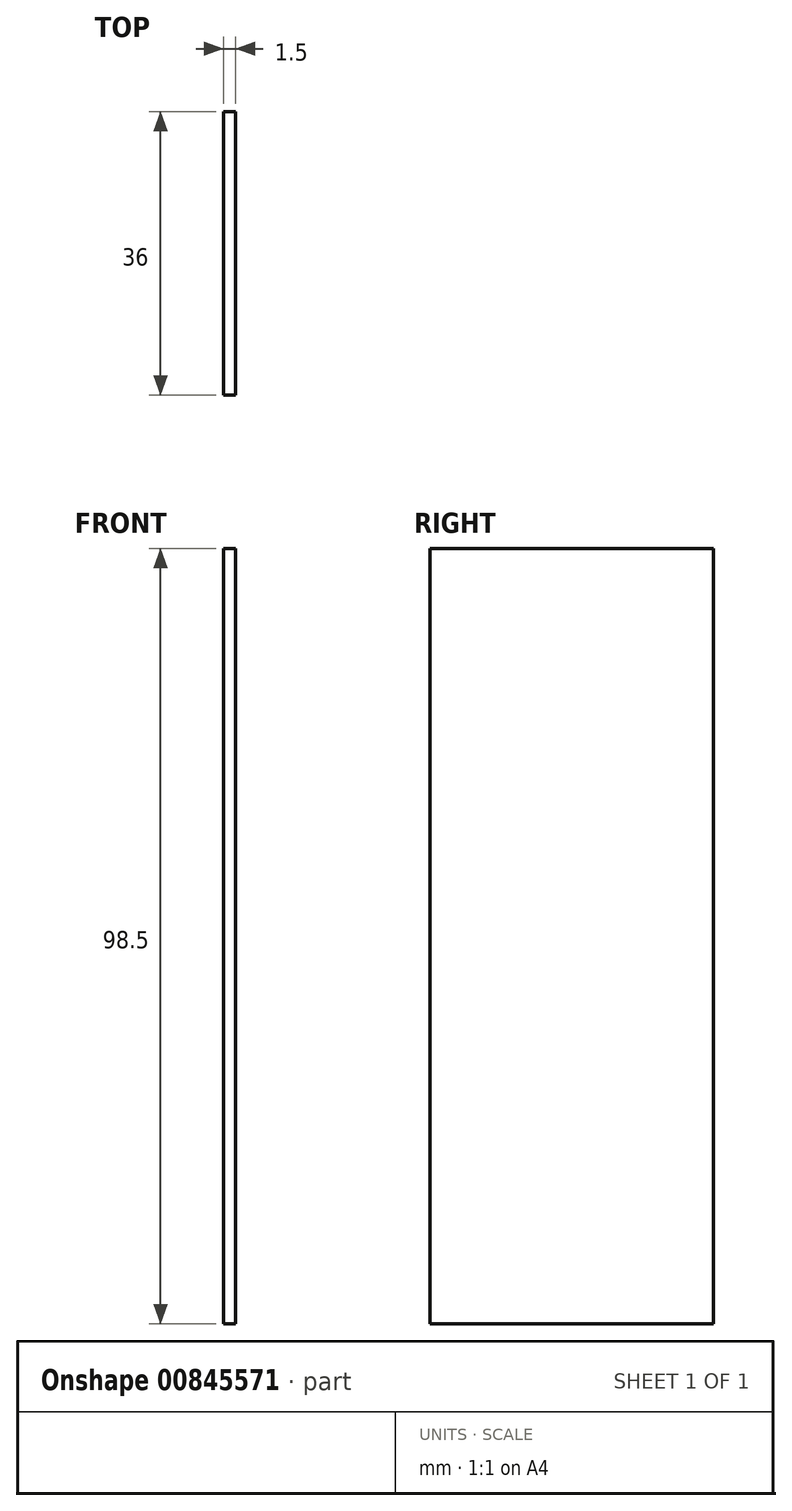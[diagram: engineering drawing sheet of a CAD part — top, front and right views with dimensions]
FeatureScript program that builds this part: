
annotation { "Feature Type Name" : "Feature", "Feature Type Description" : "" }
export const myFeature = defineFeature(function(context is Context, id is Id, definition is map)
    precondition{}
    {
        {
            var Q0;
            Q0=qCreatedBy(makeId("Top.planeOp"),FACE);
            var sketch = newSketch(context, id + "F0", { "sketchPlane" : qUnion([Q0])});
            skLineSegment(sketch, "E0.bottom", {"start": v(-33.15, 40.72) * mm, "end": v(-31.65, 40.72) * mm});
            skLineSegment(sketch, "E0.top", {"start": v(-33.15, 4.72) * mm, "end": v(-31.65, 4.72) * mm});
            skLineSegment(sketch, "E0.left", {"start": v(-33.15, 40.72) * mm, "end": v(-33.15, 4.72) * mm});
            skLineSegment(sketch, "E0.right", {"start": v(-31.65, 40.72) * mm, "end": v(-31.65, 4.72) * mm});
            skSolve(sketch);
        }
        {
            var Q0;
            Q0 = qSketchRegion(id + "F0", true);
            extrude(context, id + "F1", {"entities" : qUnion([Q0]), "depth" : 98.5 * mm, "offsetDistance" : 25 * mm});
        }
    });
